# Revit family: Plumbing-Flushometer-Sloan-Valve-Royal-111-SFSM_
name_source: partatom
category: Plumbing Fixtures
units: mm (PartAtom-declared; Revit-internal decimal feet)

## family parameters
Cut with Voids When Loaded = No
Host = Face
OmniClass Number = 23.45.05.14.99
OmniClass Title = Other Sanitary Washing Plumbing Fixtures
Part Type = Normal
Room Calculation Point = No
Round Connector Dimension = Use Diameter
Shared = No

## types (4) — shared parameters
Apparent Load = 0 VA
Assembly Code = D2020300
CW Connection = Yes
Centerline of Supply from Top of Fixture = 11 1/2"
Centerline of Supply to Centerline of Valve = 4 3/4"
Connector Description = Electrical Connection
Current = 0 A
Default Elevation = 0"
Edition number = 1
HW Connection = No
Height = 13 1/2"
Keynote = 15410
Manufacturer = Sloan Valve
Number of Poles = 1
Operating Water Pressure = 15 – 80 PSI (103 – 552 kPa)
Power Factor = 1
Product Material = Sloan Valve - Finish - Polished Chrome
Product data url = https://bimobject.com
URL = www.sloanvalve.com
Valve Pressure Drop = 0.00 psi
Vent Connection = No
Waste Connection = No
Water Inlet Connection Description = Water Inlet Connection
Water Inlet Connection Diameter = 1"
zero-valued in all types: CWFU, HWFU, WFU

## per-type parameters (varying)
| type | Description | Flush Rate | Hardwired | Number | Part Number | Voltage |
| ROYAL 111 SFSM-1.28 | 1.28 gpf, Polished Chrome Finish, Fixture Connection Top Spud, Single Flush, Battery, Royal® Exposed Sensor Water Closet Flushometer. | 1.28 gpf (4.8 Lpf) | No | 2 | 3910276 | 0 V |
| ROYAL 111 SFSM-1.6 | 1.6 gpf, Polished Chrome Finish, Fixture Connection Top Spud, Single Flush, Battery, Royal® Exposed Sensor Water Closet Flushometer | 1.6 gpf (6.0 Lpf) | No | 2 | 3910275 | 0 V |
| ROYAL 111 SFSM-1.28-HW | 1.28 gpf, Polished Chrome Finish, Fixture Connection Top Spud, Single Flush, Hardwired, Royal® Exposed Sensor Water Closet Flushometer. | 1.28 gpf (4.8 Lpf) | Yes | 3 | 3910288 | 120 V |
| ROYAL 111 SFSM-1.6-HW | 1.6 gpf, Polished Chrome Finish, Fixture Connection Top Spud, Single Flush, Hardwired, Royal® Exposed Sensor Water Closet Flushometer. | 1.6 gpf (6.0 Lpf) | Yes | 3 | 3910287 | 120 V |

note: column(s) folded — value = type name in every type: Model

## geometry (parser evidence)
native form markers: Sweep x6
no freeform markers — native parametric forms only
